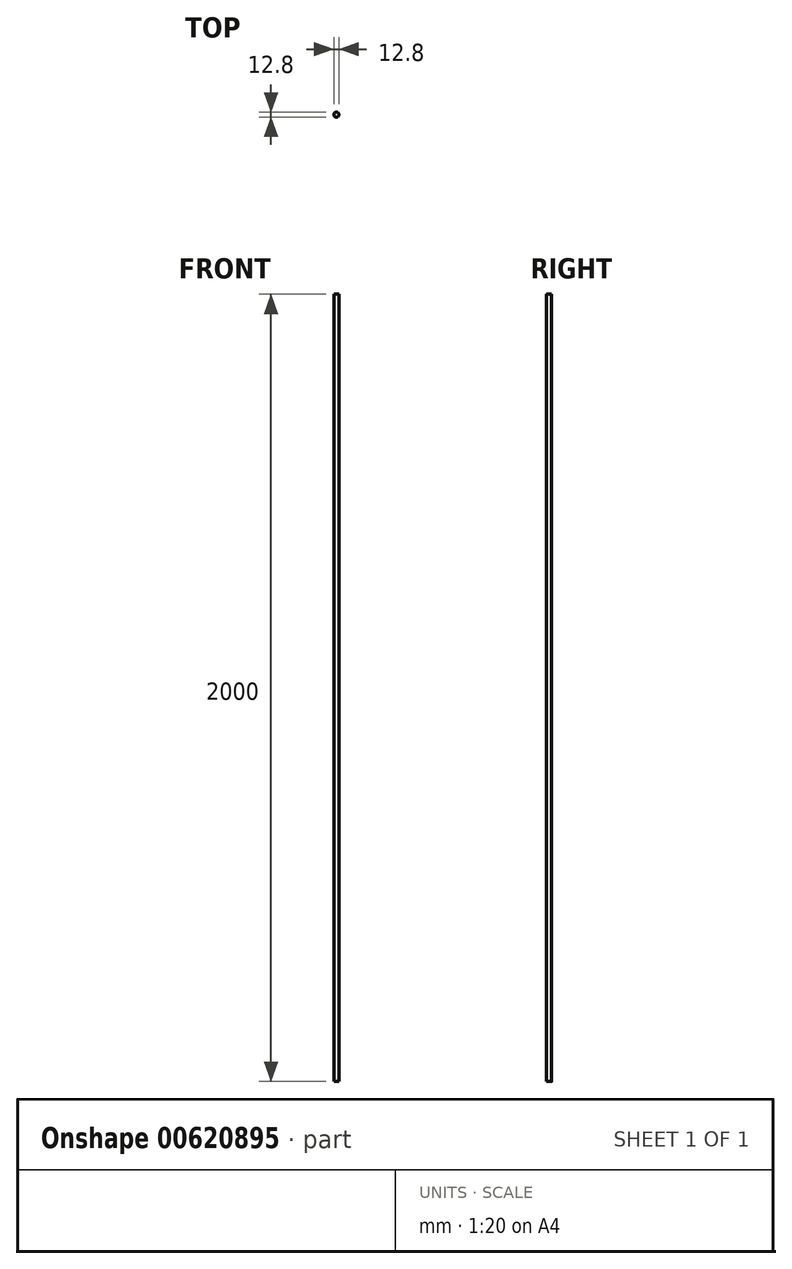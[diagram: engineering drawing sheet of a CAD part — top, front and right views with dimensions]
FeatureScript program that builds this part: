
annotation { "Feature Type Name" : "Feature", "Feature Type Description" : "" }
export const myFeature = defineFeature(function(context is Context, id is Id, definition is map)
    precondition{}
    {
        {
            var Q0;
            Q0=qCreatedBy(makeId("Top.planeOp"),FACE);
            var sketch = newSketch(context, id + "F0", { "sketchPlane" : qUnion([Q0])});
            skCircle(sketch, "E0", {"center": v(0, 0) * mm, "radius": 6.4 * mm});
            skSolve(sketch);
        }
        {
            var Q0;
            Q0=makeQuery(id+"F0.imprint","IMPRINT",FACE,{"disambiguationData":[TD([[makeQuery(id+"F0.imprint","IMPRINT",EDGE,{"derivedFrom":sQuery(id+"F0.wireOp",EDGE,"E0")}),1.0]])]});
            extrude(context, id + "F1", {"entities" : qUnion([Q0]), "depth" : 2000 * mm, "offsetDistance" : 25 * mm});
        }
    });
